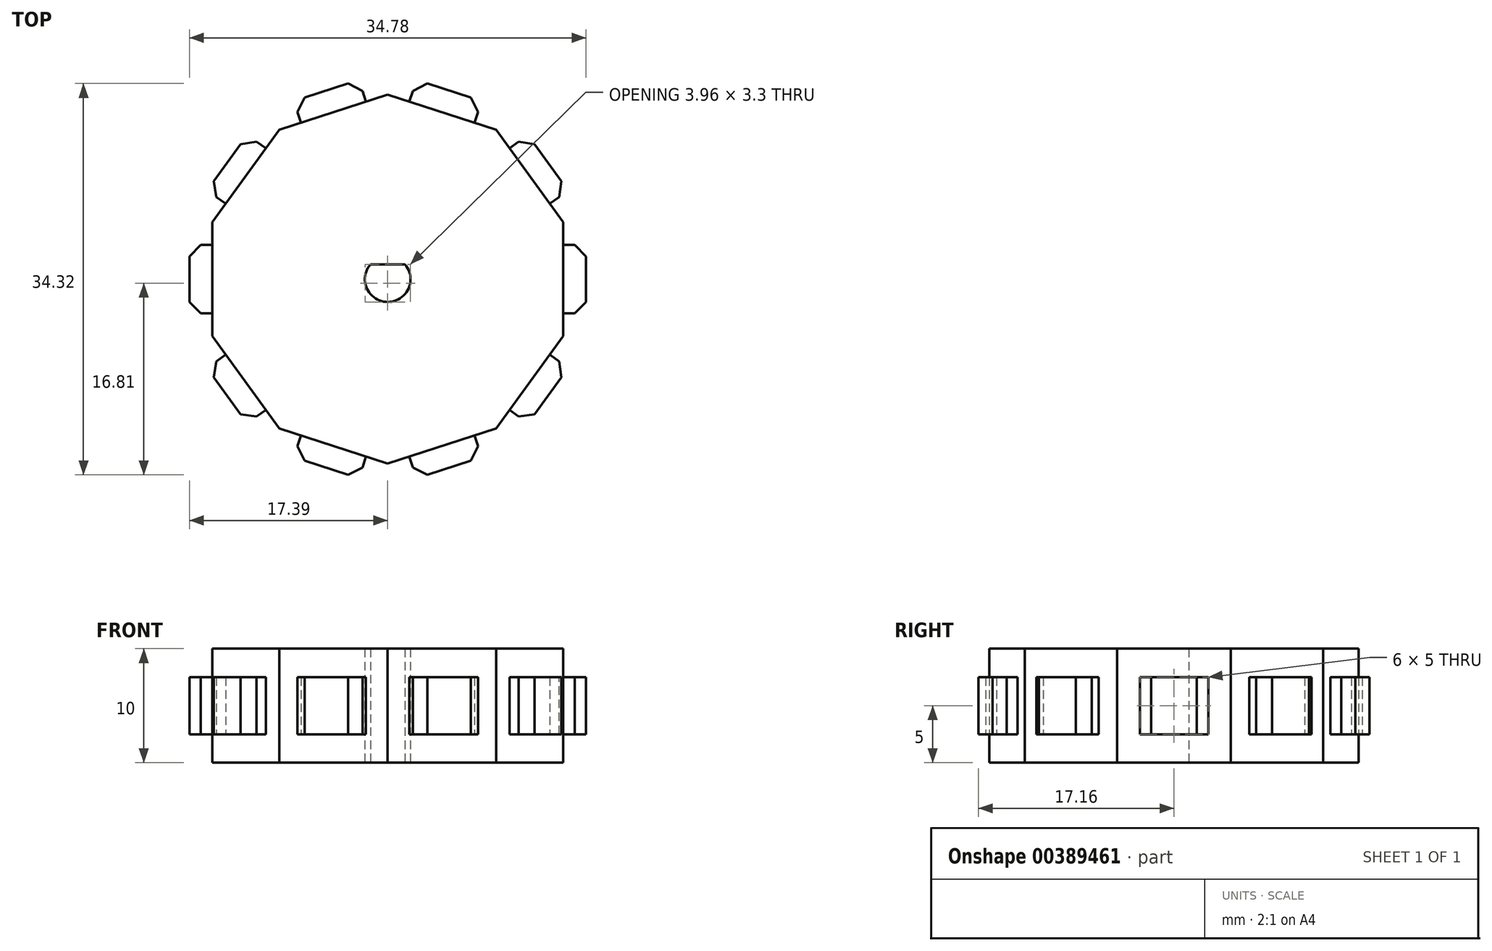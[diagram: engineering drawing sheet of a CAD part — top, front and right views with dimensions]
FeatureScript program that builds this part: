
annotation { "Feature Type Name" : "Feature", "Feature Type Description" : "" }
export const myFeature = defineFeature(function(context is Context, id is Id, definition is map)
    precondition{}
    {
        {
            var Q0;
            Q0=qCreatedBy(makeId("Top.planeOp"),FACE);
            var sketch = newSketch(context, id + "F0", { "sketchPlane" : qUnion([Q0])});
            skCircle(sketch, "E0.cCircle", {"center": v(0, 0) * mm, "radius": 16.18 * mm, "construction": true});
            skLineSegment(sketch, "E0.0", {"start": v(9.51, 13.1) * mm, "end": v(15.39, 5) * mm});
            skLineSegment(sketch, "E0.1", {"start": v(15.39, 5) * mm, "end": v(15.39, -5) * mm});
            skLineSegment(sketch, "E0.2", {"start": v(15.39, -5) * mm, "end": v(9.51, -13.1) * mm});
            skLineSegment(sketch, "E0.3", {"start": v(9.51, -13.1) * mm, "end": v(0, -16.18) * mm});
            skLineSegment(sketch, "E0.4", {"start": v(0, -16.18) * mm, "end": v(-9.51, -13.1) * mm});
            skLineSegment(sketch, "E0.5", {"start": v(-9.51, -13.1) * mm, "end": v(-15.39, -5) * mm});
            skLineSegment(sketch, "E0.6", {"start": v(-15.39, -5) * mm, "end": v(-15.39, 5) * mm});
            skLineSegment(sketch, "E0.7", {"start": v(-15.39, 5) * mm, "end": v(-9.51, 13.1) * mm});
            skLineSegment(sketch, "E0.8", {"start": v(-9.51, 13.1) * mm, "end": v(0, 16.18) * mm});
            skLineSegment(sketch, "E0.9", {"start": v(0, 16.18) * mm, "end": v(9.51, 13.1) * mm});
            skArc(sketch, "E1", {"start": v(-1.52, 1.3) * mm, "mid": v(0, -2) * mm, "end": v(1.52, 1.3) * mm});
            skLineSegment(sketch, "E2", {"start": v(-1.52, 1.3) * mm, "end": v(1.52, 1.3) * mm});
            skSolve(sketch);
        }
        {
            var Q0;
            Q0=qSketchRegion(id+"F0",true);
            extrude(context, id + "F1", {"entities" : qUnion([Q0]), "endBound" : BoundingType.SYMMETRIC, "depth" : 10 * mm});
        }
        {
            var Q0;
            Q0=qCreatedBy(makeId("Top.planeOp"),FACE);
            var sketch = newSketch(context, id + "F2", { "sketchPlane" : qUnion([Q0])});
            skLineSegment(sketch, "E3.bottom", {"start": v(17.39, 3) * mm, "end": v(15.39, 3) * mm});
            skLineSegment(sketch, "E3.top", {"start": v(17.39, -3) * mm, "end": v(15.39, -3) * mm});
            skLineSegment(sketch, "E3.left", {"start": v(17.39, 3) * mm, "end": v(17.39, -3) * mm});
            skPoint(sketch, "E3.middle", {"position": v(15.39, 0) * mm});
            skLineSegment(sketch, "E4", {"start": v(15.39, 3) * mm, "end": v(15.39, -3) * mm});
            skLineSegment(sketch, "E5.1.0", {"start": v(12.3, 12.65) * mm, "end": v(10.69, 11.47) * mm});
            skLineSegment(sketch, "E5.1.1", {"start": v(12.3, 12.65) * mm, "end": v(15.83, 7.8) * mm});
            skLineSegment(sketch, "E5.1.2", {"start": v(10.69, 11.47) * mm, "end": v(14.21, 6.62) * mm});
            skLineSegment(sketch, "E5.1.3", {"start": v(15.83, 7.8) * mm, "end": v(14.21, 6.62) * mm});
            skLineSegment(sketch, "E5.2.0", {"start": v(2.52, 17.46) * mm, "end": v(1.9, 15.56) * mm});
            skLineSegment(sketch, "E5.2.1", {"start": v(2.52, 17.46) * mm, "end": v(8.23, 15.61) * mm});
            skLineSegment(sketch, "E5.2.2", {"start": v(1.9, 15.56) * mm, "end": v(7.6, 13.7) * mm});
            skLineSegment(sketch, "E5.2.3", {"start": v(8.23, 15.61) * mm, "end": v(7.6, 13.7) * mm});
            skLineSegment(sketch, "E5.3.0", {"start": v(-8.23, 15.61) * mm, "end": v(-7.6, 13.7) * mm});
            skLineSegment(sketch, "E5.3.1", {"start": v(-8.23, 15.61) * mm, "end": v(-2.52, 17.46) * mm});
            skLineSegment(sketch, "E5.3.2", {"start": v(-7.6, 13.7) * mm, "end": v(-1.9, 15.56) * mm});
            skLineSegment(sketch, "E5.3.3", {"start": v(-2.52, 17.46) * mm, "end": v(-1.9, 15.56) * mm});
            skLineSegment(sketch, "E5.4.0", {"start": v(-15.83, 7.8) * mm, "end": v(-14.21, 6.62) * mm});
            skLineSegment(sketch, "E5.4.1", {"start": v(-15.83, 7.8) * mm, "end": v(-12.3, 12.65) * mm});
            skLineSegment(sketch, "E5.4.2", {"start": v(-14.21, 6.62) * mm, "end": v(-10.69, 11.47) * mm});
            skLineSegment(sketch, "E5.4.3", {"start": v(-12.3, 12.65) * mm, "end": v(-10.69, 11.47) * mm});
            skLineSegment(sketch, "E5.5.0", {"start": v(-17.39, -3) * mm, "end": v(-15.39, -3) * mm});
            skLineSegment(sketch, "E5.5.1", {"start": v(-17.39, -3) * mm, "end": v(-17.39, 3) * mm});
            skLineSegment(sketch, "E5.5.2", {"start": v(-15.39, -3) * mm, "end": v(-15.39, 3) * mm});
            skLineSegment(sketch, "E5.5.3", {"start": v(-17.39, 3) * mm, "end": v(-15.39, 3) * mm});
            skLineSegment(sketch, "E5.6.0", {"start": v(-12.3, -12.65) * mm, "end": v(-10.69, -11.47) * mm});
            skLineSegment(sketch, "E5.6.1", {"start": v(-12.3, -12.65) * mm, "end": v(-15.83, -7.8) * mm});
            skLineSegment(sketch, "E5.6.2", {"start": v(-10.69, -11.47) * mm, "end": v(-14.21, -6.62) * mm});
            skLineSegment(sketch, "E5.6.3", {"start": v(-15.83, -7.8) * mm, "end": v(-14.21, -6.62) * mm});
            skLineSegment(sketch, "E5.7.0", {"start": v(-2.52, -17.46) * mm, "end": v(-1.9, -15.56) * mm});
            skLineSegment(sketch, "E5.7.1", {"start": v(-2.52, -17.46) * mm, "end": v(-8.23, -15.61) * mm});
            skLineSegment(sketch, "E5.7.2", {"start": v(-1.9, -15.56) * mm, "end": v(-7.6, -13.7) * mm});
            skLineSegment(sketch, "E5.7.3", {"start": v(-8.23, -15.61) * mm, "end": v(-7.6, -13.7) * mm});
            skLineSegment(sketch, "E5.8.0", {"start": v(8.23, -15.61) * mm, "end": v(7.6, -13.7) * mm});
            skLineSegment(sketch, "E5.8.1", {"start": v(8.23, -15.61) * mm, "end": v(2.52, -17.46) * mm});
            skLineSegment(sketch, "E5.8.2", {"start": v(7.6, -13.7) * mm, "end": v(1.9, -15.56) * mm});
            skLineSegment(sketch, "E5.8.3", {"start": v(2.52, -17.46) * mm, "end": v(1.9, -15.56) * mm});
            skLineSegment(sketch, "E5.9.0", {"start": v(15.83, -7.8) * mm, "end": v(14.21, -6.62) * mm});
            skLineSegment(sketch, "E5.9.1", {"start": v(15.83, -7.8) * mm, "end": v(12.3, -12.65) * mm});
            skLineSegment(sketch, "E5.9.2", {"start": v(14.21, -6.62) * mm, "end": v(10.69, -11.47) * mm});
            skLineSegment(sketch, "E5.9.3", {"start": v(12.3, -12.65) * mm, "end": v(10.69, -11.47) * mm});
            skPoint(sketch, "E5.center", {"position": v(0, 0) * mm});
            skSolve(sketch);
        }
        {
            var Q0;
            Q0=qSketchRegion(id+"F2",true);
            extrude(context, id + "F3", {"entities" : qUnion([Q0]), "operationType" : NewBodyOperationType.ADD, "endBound" : BoundingType.SYMMETRIC, "depth" : 5 * mm});
        }
        {
            var Q0;
            Q0=makeQuery(id+"F3.opExtrude","SWEPT_EDGE",EDGE,{"disambiguationData":[OSD([sQuery(id+"F2.wireOp",EDGE,"E5.9.1"),sQuery(id+"F2.wireOp",EDGE,"E5.9.3")])]});
            var Q1;
            Q1=makeQuery(id+"F3.opExtrude","SWEPT_EDGE",EDGE,{"disambiguationData":[OSD([sQuery(id+"F2.wireOp",EDGE,"E5.9.0"),sQuery(id+"F2.wireOp",EDGE,"E5.9.1")])]});
            var Q2;
            Q2=makeQuery(id+"F3.opExtrude","SWEPT_EDGE",EDGE,{"disambiguationData":[OSD([sQuery(id+"F2.wireOp",EDGE,"E3.top"),sQuery(id+"F2.wireOp",EDGE,"E3.left")])]});
            var Q3;
            Q3=makeQuery(id+"F3.opExtrude","SWEPT_EDGE",EDGE,{"disambiguationData":[OSD([sQuery(id+"F2.wireOp",EDGE,"E3.bottom"),sQuery(id+"F2.wireOp",EDGE,"E3.left")])]});
            var Q4;
            Q4=makeQuery(id+"F3.opExtrude","SWEPT_EDGE",EDGE,{"disambiguationData":[OSD([sQuery(id+"F2.wireOp",EDGE,"E5.1.1"),sQuery(id+"F2.wireOp",EDGE,"E5.1.3")])]});
            var Q5;
            Q5=makeQuery(id+"F3.opExtrude","SWEPT_EDGE",EDGE,{"disambiguationData":[OSD([sQuery(id+"F2.wireOp",EDGE,"E5.1.0"),sQuery(id+"F2.wireOp",EDGE,"E5.1.1")])]});
            var Q6;
            Q6=makeQuery(id+"F3.opExtrude","SWEPT_EDGE",EDGE,{"disambiguationData":[OSD([sQuery(id+"F2.wireOp",EDGE,"E5.2.1"),sQuery(id+"F2.wireOp",EDGE,"E5.2.3")])]});
            var Q7;
            Q7=makeQuery(id+"F3.opExtrude","SWEPT_EDGE",EDGE,{"disambiguationData":[OSD([sQuery(id+"F2.wireOp",EDGE,"E5.2.0"),sQuery(id+"F2.wireOp",EDGE,"E5.2.1")])]});
            var Q8;
            Q8=makeQuery(id+"F3.opExtrude","SWEPT_EDGE",EDGE,{"disambiguationData":[OSD([sQuery(id+"F2.wireOp",EDGE,"E5.3.1"),sQuery(id+"F2.wireOp",EDGE,"E5.3.3")])]});
            var Q9;
            Q9=makeQuery(id+"F3.opExtrude","SWEPT_EDGE",EDGE,{"disambiguationData":[OSD([sQuery(id+"F2.wireOp",EDGE,"E5.3.0"),sQuery(id+"F2.wireOp",EDGE,"E5.3.1")])]});
            var Q10;
            Q10=makeQuery(id+"F3.opExtrude","SWEPT_EDGE",EDGE,{"disambiguationData":[OSD([sQuery(id+"F2.wireOp",EDGE,"E5.4.1"),sQuery(id+"F2.wireOp",EDGE,"E5.4.3")])]});
            var Q11;
            Q11=makeQuery(id+"F3.opExtrude","SWEPT_EDGE",EDGE,{"disambiguationData":[OSD([sQuery(id+"F2.wireOp",EDGE,"E5.4.0"),sQuery(id+"F2.wireOp",EDGE,"E5.4.1")])]});
            var Q12;
            Q12=makeQuery(id+"F3.opExtrude","SWEPT_EDGE",EDGE,{"disambiguationData":[OSD([sQuery(id+"F2.wireOp",EDGE,"E5.5.1"),sQuery(id+"F2.wireOp",EDGE,"E5.5.3")])]});
            var Q13;
            Q13=makeQuery(id+"F3.opExtrude","SWEPT_EDGE",EDGE,{"disambiguationData":[OSD([sQuery(id+"F2.wireOp",EDGE,"E5.5.0"),sQuery(id+"F2.wireOp",EDGE,"E5.5.1")])]});
            var Q14;
            Q14=makeQuery(id+"F3.opExtrude","SWEPT_EDGE",EDGE,{"disambiguationData":[OSD([sQuery(id+"F2.wireOp",EDGE,"E5.6.1"),sQuery(id+"F2.wireOp",EDGE,"E5.6.3")])]});
            var Q15;
            Q15=makeQuery(id+"F3.opExtrude","SWEPT_EDGE",EDGE,{"disambiguationData":[OSD([sQuery(id+"F2.wireOp",EDGE,"E5.6.0"),sQuery(id+"F2.wireOp",EDGE,"E5.6.1")])]});
            var Q16;
            Q16=makeQuery(id+"F3.opExtrude","SWEPT_EDGE",EDGE,{"disambiguationData":[OSD([sQuery(id+"F2.wireOp",EDGE,"E5.7.0"),sQuery(id+"F2.wireOp",EDGE,"E5.7.1")])]});
            var Q17;
            Q17=makeQuery(id+"F3.opExtrude","SWEPT_EDGE",EDGE,{"disambiguationData":[OSD([sQuery(id+"F2.wireOp",EDGE,"E5.7.1"),sQuery(id+"F2.wireOp",EDGE,"E5.7.3")])]});
            var Q18;
            Q18=makeQuery(id+"F3.opExtrude","SWEPT_EDGE",EDGE,{"disambiguationData":[OSD([sQuery(id+"F2.wireOp",EDGE,"E5.8.0"),sQuery(id+"F2.wireOp",EDGE,"E5.8.1")])]});
            var Q19;
            Q19=makeQuery(id+"F3.opExtrude","SWEPT_EDGE",EDGE,{"disambiguationData":[OSD([sQuery(id+"F2.wireOp",EDGE,"E5.8.1"),sQuery(id+"F2.wireOp",EDGE,"E5.8.3")])]});
            chamfer(context, id + "F4", {"entities" : qUnion([Q0, Q1, Q2, Q3, Q4, Q5, Q6, Q7, Q8, Q9, Q10, Q11, Q12, Q13, Q14, Q15, Q16, Q17, Q18, Q19]), "width" : 1 * mm, "tangentPropagation" : true});
        }
    });
